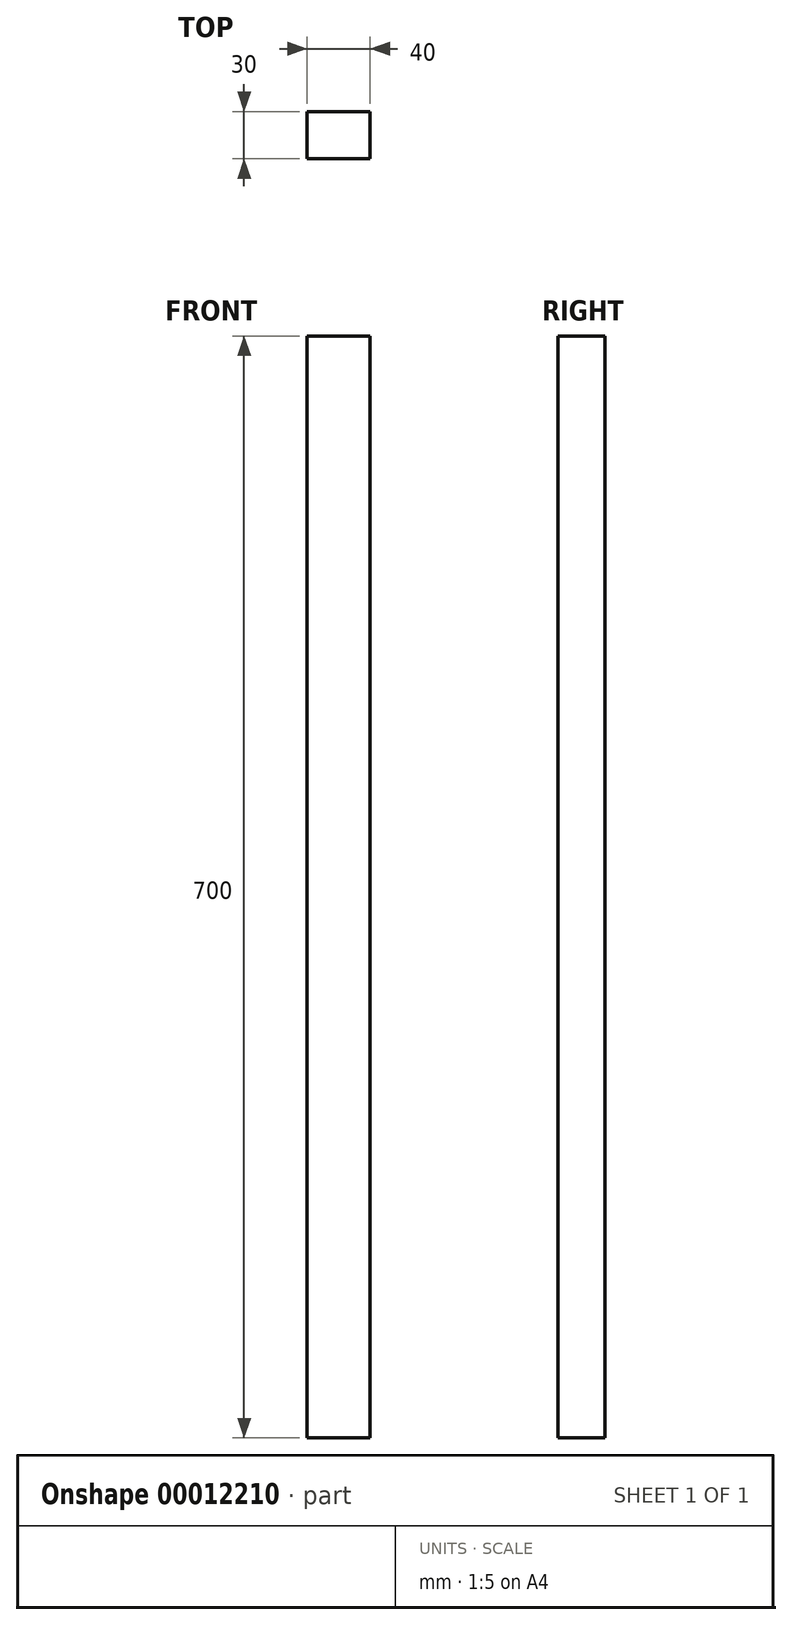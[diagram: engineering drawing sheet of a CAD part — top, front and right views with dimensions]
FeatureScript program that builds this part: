
annotation { "Feature Type Name" : "Feature", "Feature Type Description" : "" }
export const myFeature = defineFeature(function(context is Context, id is Id, definition is map)
    precondition{}
    {
        {
            var Q0;
            Q0=qCreatedBy(makeId("Top.planeOp"),FACE);
            var sketch = newSketch(context, id + "F0", { "sketchPlane" : qUnion([Q0])});
            skLineSegment(sketch, "E0.bottom", {"start": v(0, 30) * mm, "end": v(40, 30) * mm});
            skLineSegment(sketch, "E0.top", {"start": v(0, 0) * mm, "end": v(40, 0) * mm});
            skLineSegment(sketch, "E0.left", {"start": v(0, 30) * mm, "end": v(0, 0) * mm});
            skLineSegment(sketch, "E0.right", {"start": v(40, 30) * mm, "end": v(40, 0) * mm});
            skSolve(sketch);
        }
        {
            assignVariable(context, id + "F1", {"name" : "PostHightLow", "anyValue" : 700});
        }
        {
            var Q0;
            Q0=makeQuery(id+"F0.imprint","IMPRINT",FACE,{"disambiguationData":[TD([[makeQuery(id+"F0.imprint","IMPRINT",EDGE,{"derivedFrom":sQuery(id+"F0.wireOp",EDGE,"E0.bottom")}),-1.0]])]});
            extrude(context, id + "F2", {"entities" : qUnion([Q0]), "depth" : (getVariable(context, 'PostHightLow')) * mm});
        }
    });
